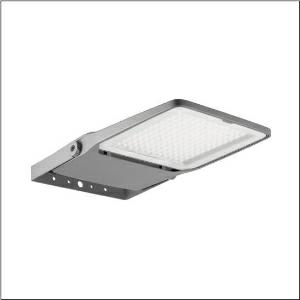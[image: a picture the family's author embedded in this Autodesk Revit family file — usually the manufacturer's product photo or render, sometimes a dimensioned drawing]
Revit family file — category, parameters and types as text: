
# Revit family: floodlight_fl_20_midi___pl43_5xa7682d2a2ac_b3e1
name_source: partatom
category: Lighting Fixtures
units: mm (PartAtom-declared; Revit-internal decimal feet)

## family parameters
Cut with Voids When Loaded = No
Host = Face
Light Source = No
Part Type = Normal
Room Calculation Point = No
Round Connector Dimension = Use Diameter
Shared = No

## types (1)
- --- (1 x LED 4000K / CRI = 70 (unbekannt), 19080 lm, 4000K)
    Apparent Load = 142 VA
    CIE Flux Codes = 32 74 99 100 100
    Color Rendering = 70
    Color Temperature = 4000K
    Default Elevation = 1800 mm
    Description = Floodlight FL 20 midi, floodlight, primary light control with lens, of plastic, primary optical cover: protective disc, of toughened safety glass, transparent, light distribution: PL43, light emission: direct distribution, primary light characteristic: asymmetric, installation type: surface-mounted, LED High Power LED, rated luminous flux: 19.080 lm, light colour: 740, colour temperature: 4000K, control gear: ECG Plus, control: flexible luminous flux parameterisation, time-dependent luminous flux control, digital communication interface, power reduction, overheat protection, electronic power reduction, with terminal, 5-pole, max. 2.5mm², mains connection: 220..240V, AC, 50/60Hz, rated input power: 142W, LED unit, of diecast aluminium, powder-coated, Siteco® metallic grey (DB 702S), length: 731 mm, width: 450 mm, height: 76mm, housing frame, of diecast aluminium, powder-coated, Siteco® metallic grey (DB 702S), wall fastening, of steel, powder-coated, Siteco® metallic grey (DB 702S), DALIprotection rating (complete): IP66, insulation class (complete): insulation class II (safety insulation), certification: CE, ENEC, VDE, protection symbol: D, permissible ambient temperature for indoor applications: -40..+40°C, permissible ambient temperature for outdoor applications: -40..+50°C, standard: DIN EN 12944, packaging unit: 1 piece

Light Distribution: PL43
    Height = 76 mm
    Lamp = 1 x LED 4000K / CRI >= 70 (unbekannt)
    Lamp Light Flux = 19080 lm
    Lamp count = 1
    Length = 731 mm
    Luminous efficacy = 134 lm/W
    Manufacturer = Siteco
    ModVariant = No
    Model = 5XA7682D2A2AC
    Number of Poles = 1
    OnlyDefault = Yes
    Power Factor = 1
    Product Name = Floodlight FL 20 midi | PL43
    Product group = floodlight | pylon top
    ProductGroupID = 6101
    Protection Class = Protection class II
    Protection Degree = IP 66
    RLX_Detail_Level = 1
    RlxData = <blob elided: 91689 chars, md5=7b5e794f>
    Socket = socket
    Standby Power = 0 W
    System Light Flux = 19080 lm
    System Power = 142 W
    Type Comments = factory setting: luminous flux: 100 % | dim-lin: 254 | 489 mA
    Type Image = l_1005944.jpg
    URL = http://relux.com
    VarID = @adj_143983
    Voltage = 0 V
    Weight = 0.00 kg
    Width = 450 mm

## geometry (parser evidence)
native form markers: Blend x4, Sweep x12
no freeform markers — native parametric forms only
